# Revit family: 201_86bcbae6bb084f1e9466377176f8b2
name_source: partatom
category: Air Terminals
revit_build: Autodesk Revit 2018 (Build: 20170223_1515(x64)
units: mm (PartAtom-declared; Revit-internal decimal feet)

## family parameters
Always vertical = Yes
Cut with Voids When Loaded = No
Part Type = Normal
Room Calculation Point = Yes
Round Connector Dimension = Use Diameter
Shared = No
Work Plane-Based = No

## types (1)
- 100-09843
    CLBTZ = 0 mm  [stored 0 ft]
    CL_Location_5000 = 5000 mm  [stored 16.4042 ft]
    D = 100 mm
    Description = Supply valve OPTR
    H_ARR = 0 mm  [stored 0 ft]
    L = 35 mm  [stored 0.114829 ft]
    L_ARR = 400 mm  [stored 1.31234 ft]
    MC Product Code = 100-09843
    Manufacturer = Flexit
    QmdConnectorList = 201;D
    R = 10 mm  [stored 0.0328084 ft]
    W_ARR = 400 mm  [stored 1.31234 ft]
    Y1 = 100 mm  [stored 0.328084 ft]
    Z1 = 65 mm  [stored 0.213255 ft]
    magiPartTypeId = 201
    magiProductFamilyId = 86bcbae6bb084f1e9466377176f8b2
    magiProductId = 9185bf8e819a4329bbb6466e1bfa9f

note: [stored X ft] marks values corroborated as IEEE doubles in the binary element streams (Revit-internal decimal feet)

## geometry (parser evidence)
native form markers: Sweep x1
no freeform markers — native parametric forms only
